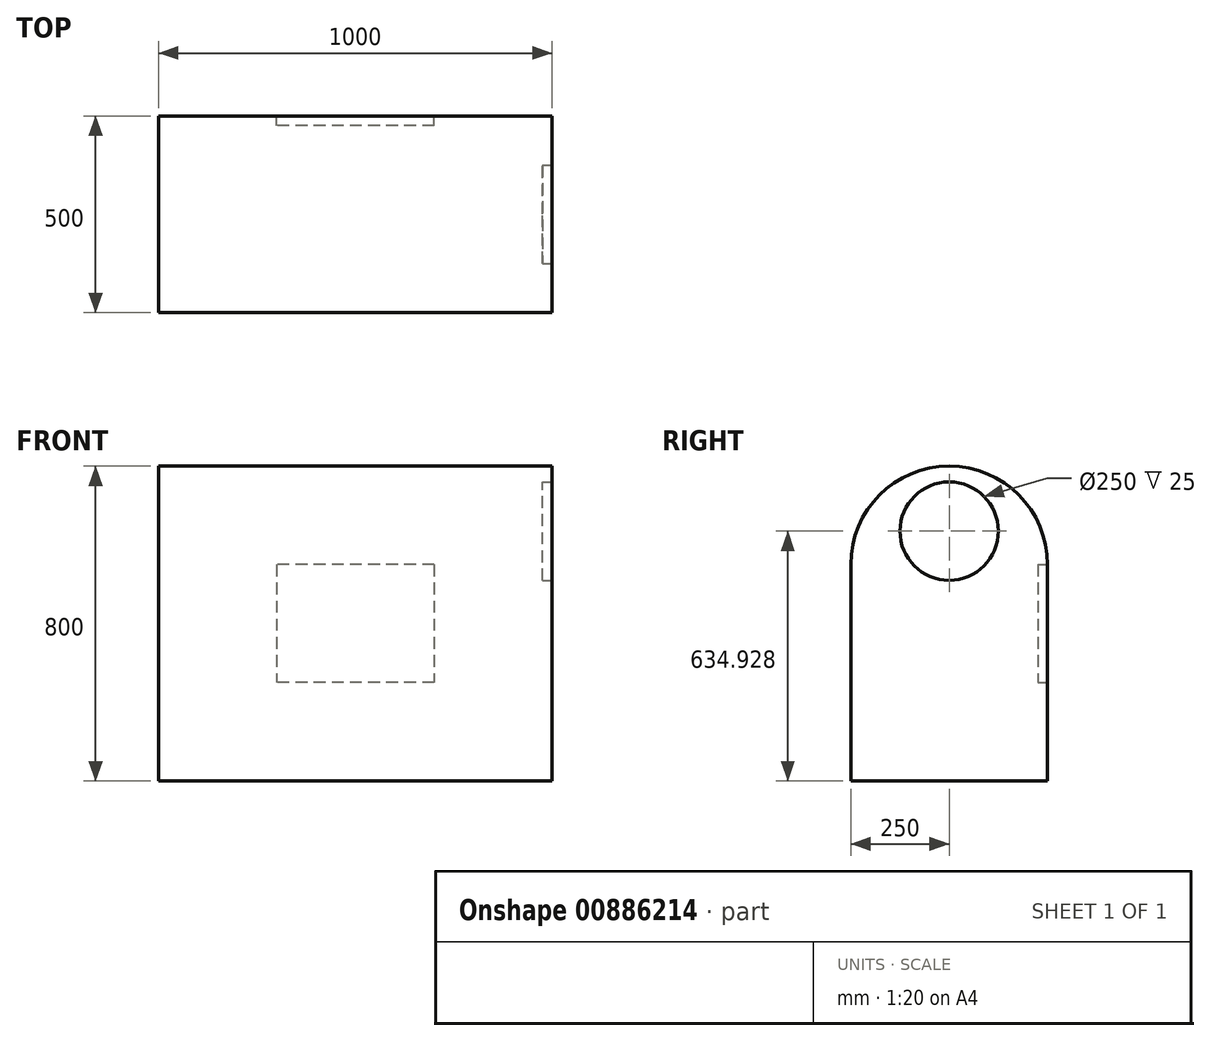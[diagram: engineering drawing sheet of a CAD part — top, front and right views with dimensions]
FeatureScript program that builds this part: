
annotation { "Feature Type Name" : "Feature", "Feature Type Description" : "" }
export const myFeature = defineFeature(function(context is Context, id is Id, definition is map)
    precondition{}
    {
        {
            var Q0;
            Q0=qCreatedBy(makeId("Right.planeOp"),FACE);
            var sketch = newSketch(context, id + "F0", { "sketchPlane" : qUnion([Q0])});
            skLineSegment(sketch, "E0.bottom", {"start": v(250, -400) * mm, "end": v(-250, -400) * mm});
            skLineSegment(sketch, "E0.top", {"start": v(250, 400) * mm, "end": v(-250, 400) * mm});
            skLineSegment(sketch, "E0.left", {"start": v(250, -400) * mm, "end": v(250, 400) * mm});
            skLineSegment(sketch, "E0.right", {"start": v(-250, -400) * mm, "end": v(-250, 400) * mm});
            skPoint(sketch, "E0.middle", {"position": v(0, 0) * mm});
            skSolve(sketch);
        }
        {
            var Q0;
            Q0 = qSketchRegion(id + "F0", true);
            extrude(context, id + "F1", {"entities" : qUnion([Q0]), "depth" : 1000 * mm, "offsetDistance" : 25 * mm});
        }
        {
            var Q0;
            Q0=makeQuery(id+"F1.opExtrude","CAP_FACE",FACE,{"disambiguationData":[OSD([sQuery(id+"F0.wireOp",EDGE,"E0.bottom"),sQuery(id+"F0.wireOp",EDGE,"E0.top"),sQuery(id+"F0.wireOp",EDGE,"E0.left"),sQuery(id+"F0.wireOp",EDGE,"E0.right")])],"isStart":false});
            var sketch = newSketch(context, id + "F2", { "sketchPlane" : qUnion([Q0])});
            skCircle(sketch, "E1", {"center": v(0, 234.93) * mm, "radius": 125 * mm});
            skPoint(sketch, "E1.centerSnap0", {"position": v(0, 400) * mm});
            skSolve(sketch);
        }
        {
            var Q0;
            Q0 = qSketchRegion(id + "F2", true);
            extrude(context, id + "F3", {"entities" : qUnion([Q0]), "operationType" : NewBodyOperationType.REMOVE, "oppositeDirection" : true, "depth" : 25 * mm, "offsetDistance" : 25 * mm});
        }
        {
            var Q0;
            Q0=makeQuery(id+"F1.opExtrude","SWEPT_EDGE",EDGE,{"disambiguationData":[OSD([sQuery(id+"F0.wireOp",EDGE,"E0.top"),sQuery(id+"F0.wireOp",EDGE,"E0.left")])]});
            var Q1;
            Q1=makeQuery(id+"F1.opExtrude","SWEPT_EDGE",EDGE,{"disambiguationData":[OSD([sQuery(id+"F0.wireOp",EDGE,"E0.top"),sQuery(id+"F0.wireOp",EDGE,"E0.right")])]});
            fillet(context, id + "F4", {"entities" : qUnion([Q0, Q1]), "radius" : 250 * mm, "tangentPropagation" : true, "allowEdgeOverflow" : false});
        }
        {
            var Q0;
            Q0=makeQuery(id+"F1.opExtrude","SWEPT_FACE",FACE,{"disambiguationData":[OSD([sQuery(id+"F0.wireOp",EDGE,"E0.left")])]});
            var sketch = newSketch(context, id + "F5", { "sketchPlane" : qUnion([Q0])});
            skLineSegment(sketch, "E2.bottom", {"start": v(-701.97, -14.34) * mm, "end": v(-698.03, -14.34) * mm});
            skLineSegment(sketch, "E2.top", {"start": v(-701.97, 314.34) * mm, "end": v(-698.03, 314.34) * mm});
            skPoint(sketch, "E2.middle", {"position": v(-700, 150) * mm});
            skLineSegment(sketch, "E3.bottom", {"start": v(-700, 150) * mm, "end": v(-300, 150) * mm});
            skLineSegment(sketch, "E3.top", {"start": v(-700, -150) * mm, "end": v(-300, -150) * mm});
            skLineSegment(sketch, "E3.left", {"start": v(-700, 150) * mm, "end": v(-700, -150) * mm});
            skLineSegment(sketch, "E3.right", {"start": v(-300, 150) * mm, "end": v(-300, -150) * mm});
            skSolve(sketch);
        }
        {
            var Q0;
            {var subQ3=sQuery(id+"F5.wireOp",EDGE,"E3.bottom");Q0=makeQuery(id+"F5.imprint","IMPRINT",FACE,{"disambiguationData":[TD([[makeQuery(id+"F5.imprint","IMPRINT",EDGE,{"derivedFrom":subQ3}),1.0]])]});}
            extrude(context, id + "F6", {"entities" : qUnion([Q0]), "operationType" : NewBodyOperationType.REMOVE, "oppositeDirection" : true, "depth" : 25 * mm, "offsetDistance" : 25 * mm});
        }
        {
            var Q0;
            Q0=makeQuery(id+"F1.opExtrude","SWEPT_FACE",FACE,{"disambiguationData":[OSD([sQuery(id+"F0.wireOp",EDGE,"E0.left")])]});
            var sketch = newSketch(context, id + "F7", { "sketchPlane" : qUnion([Q0])});
            skLineSegment(sketch, "E4.bottom", {"start": v(-200, -408.03) * mm, "end": v(-800, -408.03) * mm});
            skLineSegment(sketch, "E4.top", {"start": v(-200, -308.03) * mm, "end": v(-800, -308.03) * mm});
            skLineSegment(sketch, "E4.left", {"start": v(-200, -408.03) * mm, "end": v(-200, -308.03) * mm});
            skLineSegment(sketch, "E4.right", {"start": v(-800, -408.03) * mm, "end": v(-800, -308.03) * mm});
            skPoint(sketch, "E4.middle", {"position": v(-500, -358.03) * mm});
            skPoint(sketch, "E4.middle.positionSnap0", {"position": v(-500, -400) * mm});
            skPoint(sketch, "E4.centerSnap0", {"position": v(-500, -400) * mm});
            skSolve(sketch);
        }
        {
            var Q0;
            Q0=makeQuery(id+"F7.imprint","IMPRINT",FACE,{"disambiguationData":[TD([[makeQuery(id+"F7.imprint","IMPRINT",EDGE,{"derivedFrom":sQuery(id+"F7.wireOp",EDGE,"E4.bottom")}),-1.0]])]});
            extrude(context, id + "F8", {"entities" : qUnion([Q0]), "operationType" : NewBodyOperationType.REMOVE, "oppositeDirection" : true, "depth" : 100 * mm, "offsetDistance" : 25 * mm});
        }
    });
